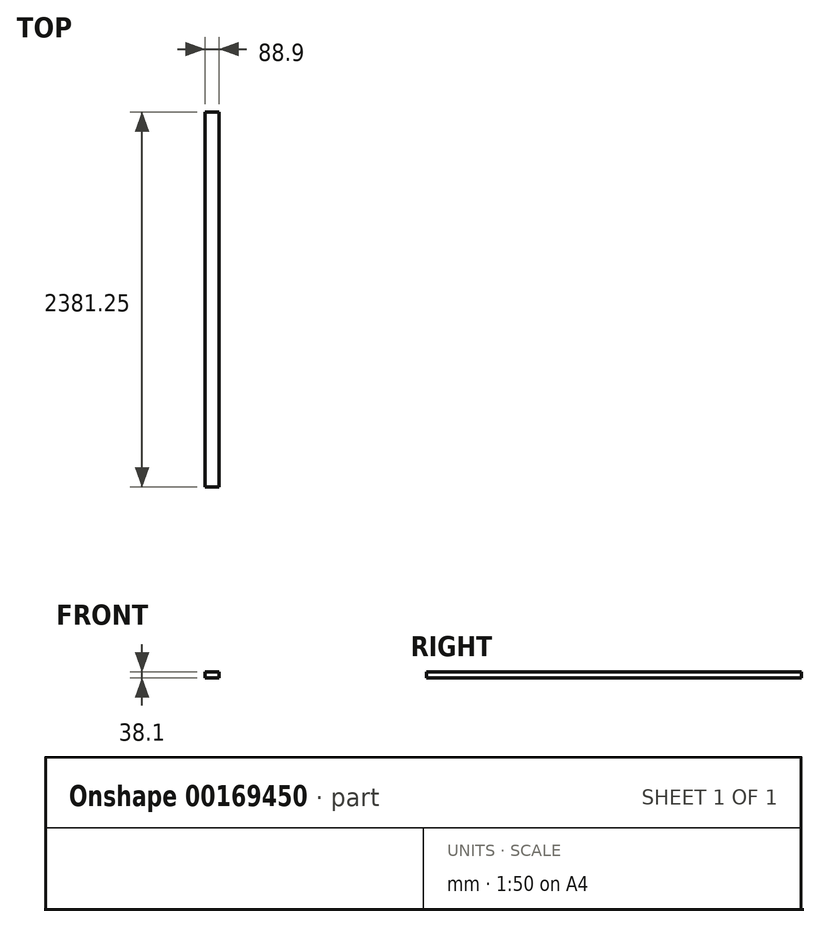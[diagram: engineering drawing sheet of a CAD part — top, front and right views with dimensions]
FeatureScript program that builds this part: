
annotation { "Feature Type Name" : "Feature", "Feature Type Description" : "" }
export const myFeature = defineFeature(function(context is Context, id is Id, definition is map)
    precondition{}
    {
        {
            var Q0;
            Q0=qCreatedBy(makeId("Front.planeOp"),FACE);
            var sketch = newSketch(context, id + "F0", { "sketchPlane" : qUnion([Q0])});
            skLineSegment(sketch, "E0.bottom", {"start": v(0, 0) * mm, "end": v(88.9, 0) * mm});
            skLineSegment(sketch, "E0.top", {"start": v(0, -38.1) * mm, "end": v(88.9, -38.1) * mm});
            skLineSegment(sketch, "E0.left", {"start": v(0, 0) * mm, "end": v(0, -38.1) * mm});
            skLineSegment(sketch, "E0.right", {"start": v(88.9, 0) * mm, "end": v(88.9, -38.1) * mm});
            skSolve(sketch);
        }
        {
            var Q0;
            Q0 = qSketchRegion(id + "F0", true);
            extrude(context, id + "F1", {"entities" : qUnion([Q0]), "depth" : 2381.25 * mm});
        }
    });
